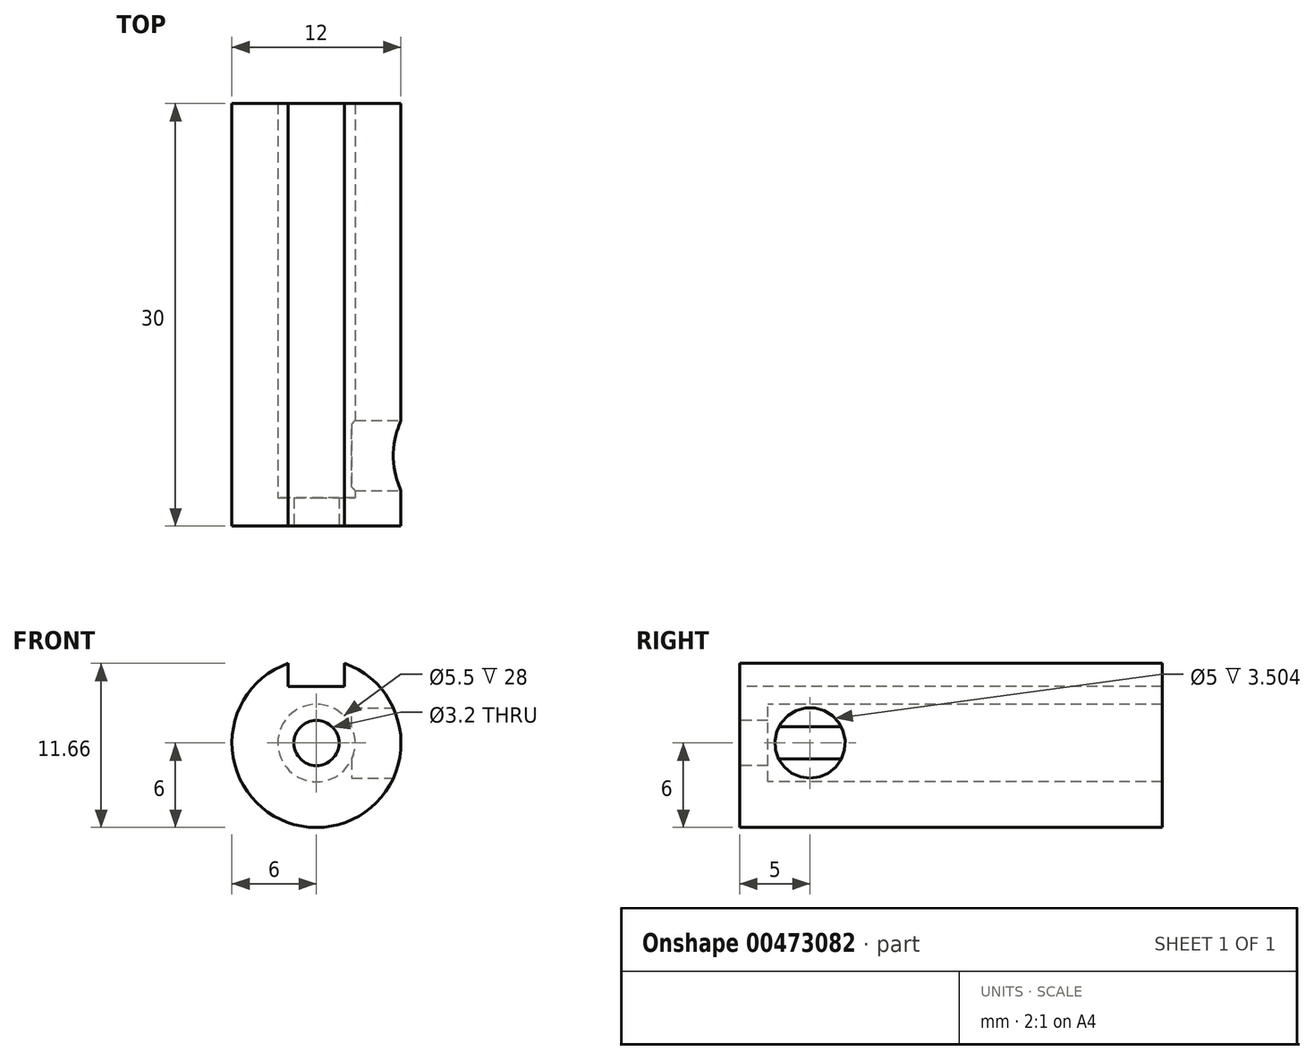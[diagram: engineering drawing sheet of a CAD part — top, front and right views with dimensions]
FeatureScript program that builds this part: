
annotation { "Feature Type Name" : "Feature", "Feature Type Description" : "" }
export const myFeature = defineFeature(function(context is Context, id is Id, definition is map)
    precondition{}
    {
        {
            var Q0;
            Q0=qCreatedBy(makeId("Front.planeOp"),FACE);
            var sketch = newSketch(context, id + "F0", { "sketchPlane" : qUnion([Q0])});
            skCircle(sketch, "E0", {"center": v(0, 0) * mm, "radius": 6 * mm});
            skSolve(sketch);
        }
        {
            var Q0;
            Q0=makeQuery(id+"F0.imprint","IMPRINT",FACE,{"disambiguationData":[TD([[makeQuery(id+"F0.imprint","IMPRINT",EDGE,{"derivedFrom":sQuery(id+"F0.wireOp",EDGE,"E0")}),1.0]])]});
            extrude(context, id + "F1", {"entities" : qUnion([Q0]), "depth" : 30 * mm});
        }
        {
            var Q0;
            Q0=makeQuery(id+"F1.opExtrude","CAP_FACE",FACE,{"disambiguationData":[OSD([sQuery(id+"F0.wireOp",EDGE,"E0")])],"isStart":false});
            var sketch = newSketch(context, id + "F2", { "sketchPlane" : qUnion([Q0])});
            skCircle(sketch, "E1", {"center": v(0, 0) * mm, "radius": 2.75 * mm});
            skSolve(sketch);
        }
        {
            var Q0;
            Q0=qSketchRegion(id+"F2",true);
            extrude(context, id + "F3", {"entities" : qUnion([Q0]), "operationType" : NewBodyOperationType.REMOVE, "endBound" : BoundingType.THROUGH_ALL, "oppositeDirection" : true, "depth" : 25 * mm});
        }
        {
            var Q0;
            Q0=qCreatedBy(makeId("Top.planeOp"),FACE);
            cPlane(context, id + "F4", {"entities" : qUnion([Q0]), "cplaneType" : CPlaneType.OFFSET, "offset" : 4 * mm, "width" : 150 * mm, "height" : 150 * mm});
        }
        {
            var Q0;
            Q0=qCreatedBy(id+"F4.planeOp",FACE);
            var Q1;
            Q1=makeQuery(id+"F1.opExtrude","CAP_EDGE",EDGE,{"disambiguationData":[OSD([sQuery(id+"F0.wireOp",EDGE,"E0")])],"isStart":false});
            cPlane(context, id + "F5", {"entities" : qUnion([Q0, Q1]), "cplaneType" : CPlaneType.LINE_ANGLE, "offset" : 25 * mm, "angle" : 45 * degree, "width" : 150 * mm, "height" : 150 * mm});
        }
        {
            var Q0;
            Q0=qCreatedBy(id+"F5.planeOp",FACE);
            cPlane(context, id + "F6", {"entities" : qUnion([Q0]), "cplaneType" : CPlaneType.OFFSET, "offset" : 3.5 * mm, "width" : 150 * mm, "height" : 150 * mm});
        }
        {
            var Q0;
            Q0=qCreatedBy(id+"F5.planeOp",FACE);
            var Q1;
            Q1=makeQuery(id+"F1.opExtrude","CAP_EDGE",EDGE,{"disambiguationData":[OSD([sQuery(id+"F0.wireOp",EDGE,"E0")])],"isStart":false});
            cPlane(context, id + "F7", {"entities" : qUnion([Q0, Q1]), "cplaneType" : CPlaneType.LINE_ANGLE, "offset" : 25 * mm, "angle" : 90 * degree, "width" : 150 * mm, "height" : 150 * mm});
        }
        {
            var Q0;
            Q0=makeQuery(id+"F1.opExtrude","CAP_FACE",FACE,{"disambiguationData":[OSD([sQuery(id+"F0.wireOp",EDGE,"E0")])],"isStart":false});
            var sketch = newSketch(context, id + "F8", { "sketchPlane" : qUnion([Q0])});
            skCircle(sketch, "E2", {"center": v(0, 0) * mm, "radius": 1.6 * mm});
            skCircle(sketch, "E3", {"center": v(0, 0) * mm, "radius": 5 * mm});
            skSolve(sketch);
        }
        {
            var Q0;
            Q0=qSketchRegion(id+"F8",true);
            extrude(context, id + "F9", {"entities" : qUnion([Q0]), "operationType" : NewBodyOperationType.ADD, "oppositeDirection" : true, "depth" : 2 * mm});
        }
        {
            var Q0;
            Q0=qCreatedBy(makeId("Right.planeOp"),FACE);
            cPlane(context, id + "F10", {"entities" : qUnion([Q0]), "cplaneType" : CPlaneType.OFFSET, "offset" : 6 * mm, "width" : 150 * mm, "height" : 150 * mm});
        }
        {
            var Q0;
            Q0=qCreatedBy(id+"F10.planeOp",FACE);
            var sketch = newSketch(context, id + "F11", { "sketchPlane" : qUnion([Q0])});
            skLineSegment(sketch, "E4.bottom", {"start": v(0, 2) * mm, "end": v(-30, 2) * mm});
            skLineSegment(sketch, "E4.top", {"start": v(0, -2) * mm, "end": v(-30, -2) * mm});
            skLineSegment(sketch, "E4.left", {"start": v(0, 2) * mm, "end": v(0, -2) * mm});
            skLineSegment(sketch, "E4.right", {"start": v(-30, 2) * mm, "end": v(-30, -2) * mm});
            skLineSegment(sketch, "E5", {"start": v(0, 0) * mm, "end": v(-30, 0) * mm, "construction": true});
            skPoint(sketch, "E5.startSnap0", {"position": v(0, 0) * mm});
            skSolve(sketch);
        }
        {
            var Q0;
            Q0=qCreatedBy(id+"F4.planeOp",FACE);
            var sketch = newSketch(context, id + "F12", { "sketchPlane" : qUnion([Q0])});
            skLineSegment(sketch, "E6.bottom", {"start": v(-2, 0) * mm, "end": v(2, 0) * mm});
            skLineSegment(sketch, "E6.top", {"start": v(-2, -30) * mm, "end": v(2, -30) * mm});
            skLineSegment(sketch, "E6.left", {"start": v(-2, 0) * mm, "end": v(-2, -30) * mm});
            skLineSegment(sketch, "E6.right", {"start": v(2, 0) * mm, "end": v(2, -30) * mm});
            skLineSegment(sketch, "E7", {"start": v(0, 0) * mm, "end": v(0, -30) * mm, "construction": true});
            skSolve(sketch);
        }
        {
            var Q0;
            Q0=qSketchRegion(id+"F12",true);
            extrude(context, id + "F13", {"entities" : qUnion([Q0]), "operationType" : NewBodyOperationType.REMOVE, "depth" : 3 * mm});
        }
        {
            var Q0;
            Q0=qCreatedBy(id+"F10.planeOp",FACE);
            var sketch = newSketch(context, id + "F14", { "sketchPlane" : qUnion([Q0])});
            skCircle(sketch, "E8", {"center": v(-25, 0) * mm, "radius": 2.5 * mm});
            skSolve(sketch);
        }
        {
            var Q0;
            Q0 = qSketchRegion(id + "F14", true);
            extrude(context, id + "F15", {"entities" : qUnion([Q0]), "operationType" : NewBodyOperationType.REMOVE, "oppositeDirection" : true, "depth" : 3.5 * mm});
        }
    });
